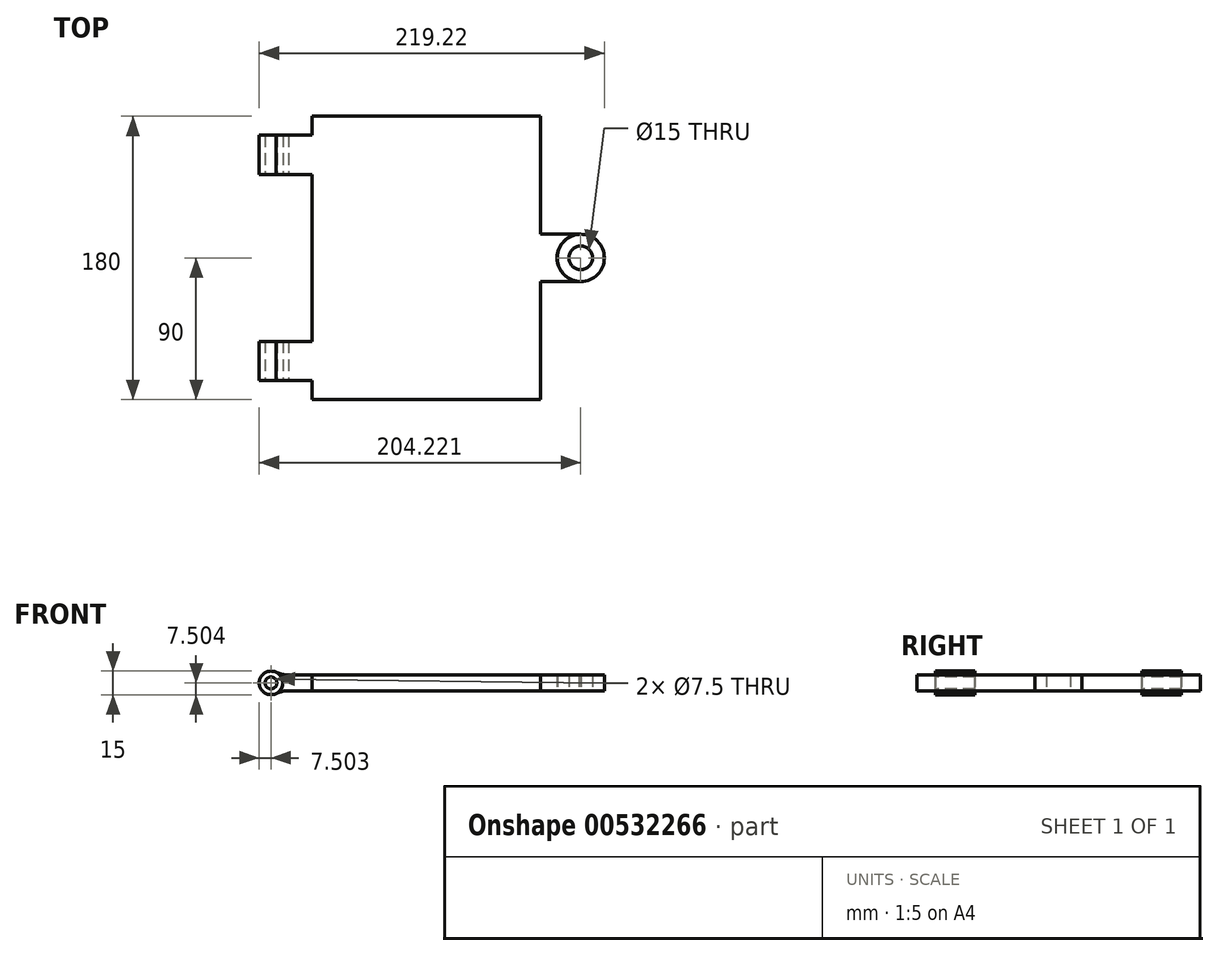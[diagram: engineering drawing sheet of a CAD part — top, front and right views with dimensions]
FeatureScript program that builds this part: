
annotation { "Feature Type Name" : "Feature", "Feature Type Description" : "" }
export const myFeature = defineFeature(function(context is Context, id is Id, definition is map)
    precondition{}
    {
        {
            var Q0;
            Q0=qCreatedBy(makeId("Top.planeOp"),FACE);
            var sketch = newSketch(context, id + "F0", { "sketchPlane" : qUnion([Q0])});
            skLineSegment(sketch, "E0.bottom", {"start": v(-72.5, 90) * mm, "end": v(72.5, 90) * mm});
            skLineSegment(sketch, "E0.top", {"start": v(-72.5, -90) * mm, "end": v(72.5, -90) * mm});
            skPoint(sketch, "E0.middle", {"position": v(0, 0) * mm});
            skLineSegment(sketch, "E1", {"start": v(-72.5, 90) * mm, "end": v(-72.5, 78) * mm});
            skLineSegment(sketch, "E2", {"start": v(-72.5, 78) * mm, "end": v(-87.5, 78) * mm});
            skLineSegment(sketch, "E3", {"start": v(-87.5, 78) * mm, "end": v(-87.5, 53) * mm});
            skLineSegment(sketch, "E4", {"start": v(-87.5, 53) * mm, "end": v(-72.5, 53) * mm});
            skLineSegment(sketch, "E5.MirrorCS", {"start": v(-72.5, -78) * mm, "end": v(-87.5, -78) * mm});
            skLineSegment(sketch, "E6.MirrorCS", {"start": v(-87.5, -78) * mm, "end": v(-87.5, -53) * mm});
            skLineSegment(sketch, "E7.MirrorCS", {"start": v(-72.5, -90) * mm, "end": v(-72.5, -78) * mm});
            skLineSegment(sketch, "E8.MirrorCS", {"start": v(-87.5, -53) * mm, "end": v(-72.5, -53) * mm});
            skLineSegment(sketch, "E9", {"start": v(-72.5, 53) * mm, "end": v(-72.5, -53) * mm});
            skLineSegment(sketch, "E10", {"start": v(72.5, 90) * mm, "end": v(72.5, 15) * mm});
            skLineSegment(sketch, "E11", {"start": v(72.5, -15) * mm, "end": v(99.43, -14.94) * mm});
            skLineSegment(sketch, "E12", {"start": v(72.5, -90) * mm, "end": v(72.5, -15) * mm});
            skLineSegment(sketch, "E13", {"start": v(83.09, 15) * mm, "end": v(98.1, 15) * mm});
            skPoint(sketch, "E14.centerSnap0", {"position": v(83.1, 0.01) * mm});
            skPoint(sketch, "E15.orphan", {"position": v(83.1, -14.98) * mm});
            skLineSegment(sketch, "E16", {"start": v(72.5, 15) * mm, "end": v(83.09, 15) * mm});
            skArc(sketch, "E17", {"start": v(98.1, 15) * mm, "mid": v(83.11, -0.67) * mm, "end": v(99.43, -14.94) * mm});
            skSolve(sketch);
        }
        {
            var Q0;
            Q0 = qSketchRegion(id + "F0", true);
            extrude(context, id + "F1", {"entities" : qUnion([Q0]), "endBound" : BoundingType.SYMMETRIC, "depth" : 10 * mm, "offsetDistance" : 25 * mm});
        }
        {
            var Q0;
            Q0=qCreatedBy(makeId("Top.planeOp"),FACE);
            var sketch = newSketch(context, id + "F2", { "sketchPlane" : qUnion([Q0])});
            skCircle(sketch, "E18", {"center": v(98.01, 0) * mm, "radius": 15 * mm});
            skCircle(sketch, "E19", {"center": v(98.01, 0) * mm, "radius": 7.5 * mm});
            skSolve(sketch);
        }
        {
            var Q0;
            Q0 = qSketchRegion(id + "F2", true);
            extrude(context, id + "F3", {"entities" : qUnion([Q0]), "endBound" : BoundingType.SYMMETRIC, "depth" : 10 * mm, "offsetDistance" : 25 * mm});
        }
        {
            var Q0;
            Q0=makeQuery(id+"F1.opExtrude","SWEPT_FACE",FACE,{"disambiguationData":[OSD([sQuery(id+"F0.wireOp",EDGE,"E5.MirrorCS")])]});
            var sketch = newSketch(context, id + "F4", { "sketchPlane" : qUnion([Q0])});
            skPoint(sketch, "E20.centerSnap0", {"position": v(-87.5, 0) * mm});
            skArc(sketch, "E21", {"start": v(-95.52, -6.84) * mm, "mid": v(-91.2, -0.02) * mm, "end": v(-95.59, 6.76) * mm});
            skArc(sketch, "E22", {"start": v(-95.59, 6.76) * mm, "mid": v(-91.64, 5.45) * mm, "end": v(-87.5, 5) * mm});
            skArc(sketch, "E23.MirrorCS", {"start": v(-95.52, -6.84) * mm, "mid": v(-91.58, -5.49) * mm, "end": v(-87.45, -5) * mm});
            skLineSegment(sketch, "E24", {"start": v(-87.5, 5) * mm, "end": v(-87.45, -5) * mm});
            skSolve(sketch);
        }
        {
            var Q0;
            Q0 = qSketchRegion(id + "F4", true);
            extrude(context, id + "F5", {"entities" : qUnion([Q0]), "operationType" : NewBodyOperationType.ADD, "depth" : -25 * mm, "offsetDistance" : 25 * mm});
        }
        {
            var Q0;
            Q0=makeQuery(id+"F1.opExtrude","SWEPT_FACE",FACE,{"disambiguationData":[OSD([sQuery(id+"F0.wireOp",EDGE,"E4")])]});
            var sketch = newSketch(context, id + "F6", { "sketchPlane" : qUnion([Q0])});
            skArc(sketch, "E25", {"start": v(-95.52, -6.84) * mm, "mid": v(-91.2, -0.02) * mm, "end": v(-95.59, 6.76) * mm});
            skArc(sketch, "E26", {"start": v(-95.59, 6.76) * mm, "mid": v(-91.64, 5.45) * mm, "end": v(-87.5, 5) * mm});
            skArc(sketch, "E27.MirrorCS", {"start": v(-95.52, -6.84) * mm, "mid": v(-91.6, -5.5) * mm, "end": v(-87.5, -5) * mm});
            skLineSegment(sketch, "E28", {"start": v(-87.5, 5) * mm, "end": v(-87.5, -5) * mm});
            skSolve(sketch);
        }
        {
            var Q0;
            Q0 = qSketchRegion(id + "F6", true);
            extrude(context, id + "F7", {"entities" : qUnion([Q0]), "operationType" : NewBodyOperationType.ADD, "depth" : -25 * mm, "offsetDistance" : 25 * mm});
        }
        {
            var Q0;
            Q0=makeQuery(id+"F5.boolean.opBoolean","MERGE",FACE,{"derivedFrom":[makeQuery(id+"F1.opExtrude","SWEPT_FACE",FACE,{"disambiguationData":[OSD([sQuery(id+"F0.wireOp",EDGE,"E5.MirrorCS")])]}),makeQuery(id+"F5.opExtrude","CAP_FACE",FACE,{"disambiguationData":[OSD([sQuery(id+"F4.wireOp",EDGE,"E21"),sQuery(id+"F4.wireOp",EDGE,"E22"),sQuery(id+"F4.wireOp",EDGE,"E23.MirrorCS"),sQuery(id+"F4.wireOp",EDGE,"E24")])],"isStart":true})]});
            var sketch = newSketch(context, id + "F8", { "sketchPlane" : qUnion([Q0])});
            skCircle(sketch, "E29", {"center": v(-98.7, -0.06) * mm, "radius": 7.5 * mm});
            skCircle(sketch, "E30", {"center": v(-98.7, -0.06) * mm, "radius": 3.75 * mm});
            skSolve(sketch);
        }
        {
            var Q0;
            Q0 = qSketchRegion(id + "F8", true);
            extrude(context, id + "F9", {"entities" : qUnion([Q0]), "depth" : -25 * mm, "offsetDistance" : 25 * mm});
        }
        {
            var Q0;
            Q0=makeQuery(id+"F7.boolean.opBoolean","MERGE",FACE,{"derivedFrom":[makeQuery(id+"F1.opExtrude","SWEPT_FACE",FACE,{"disambiguationData":[OSD([sQuery(id+"F0.wireOp",EDGE,"E4")])]}),makeQuery(id+"F7.opExtrude","CAP_FACE",FACE,{"disambiguationData":[OSD([sQuery(id+"F6.wireOp",EDGE,"E25"),sQuery(id+"F6.wireOp",EDGE,"E26"),sQuery(id+"F6.wireOp",EDGE,"E27.MirrorCS"),sQuery(id+"F6.wireOp",EDGE,"E28")])],"isStart":true})]});
            var sketch = newSketch(context, id + "F10", { "sketchPlane" : qUnion([Q0])});
            skCircle(sketch, "E31", {"center": v(-98.7, -0.06) * mm, "radius": 7.5 * mm});
            skCircle(sketch, "E32", {"center": v(-98.7, -0.06) * mm, "radius": 3.75 * mm});
            skSolve(sketch);
        }
        {
            var Q0;
            Q0 = qSketchRegion(id + "F10", true);
            extrude(context, id + "F11", {"entities" : qUnion([Q0]), "depth" : -25 * mm, "offsetDistance" : 25 * mm});
        }
        {
            var Q0;
            Q0=makeQuery(id+"F1.opExtrude","SWEPT_BODY",BODY,{"disambiguationData":[OSD([sQuery(id+"F0.wireOp",EDGE,"E11"),sQuery(id+"F0.wireOp",EDGE,"E17")])]});
            deleteBodies(context, id + "F12", {"entities" : qUnion([Q0])});
        }
    });
